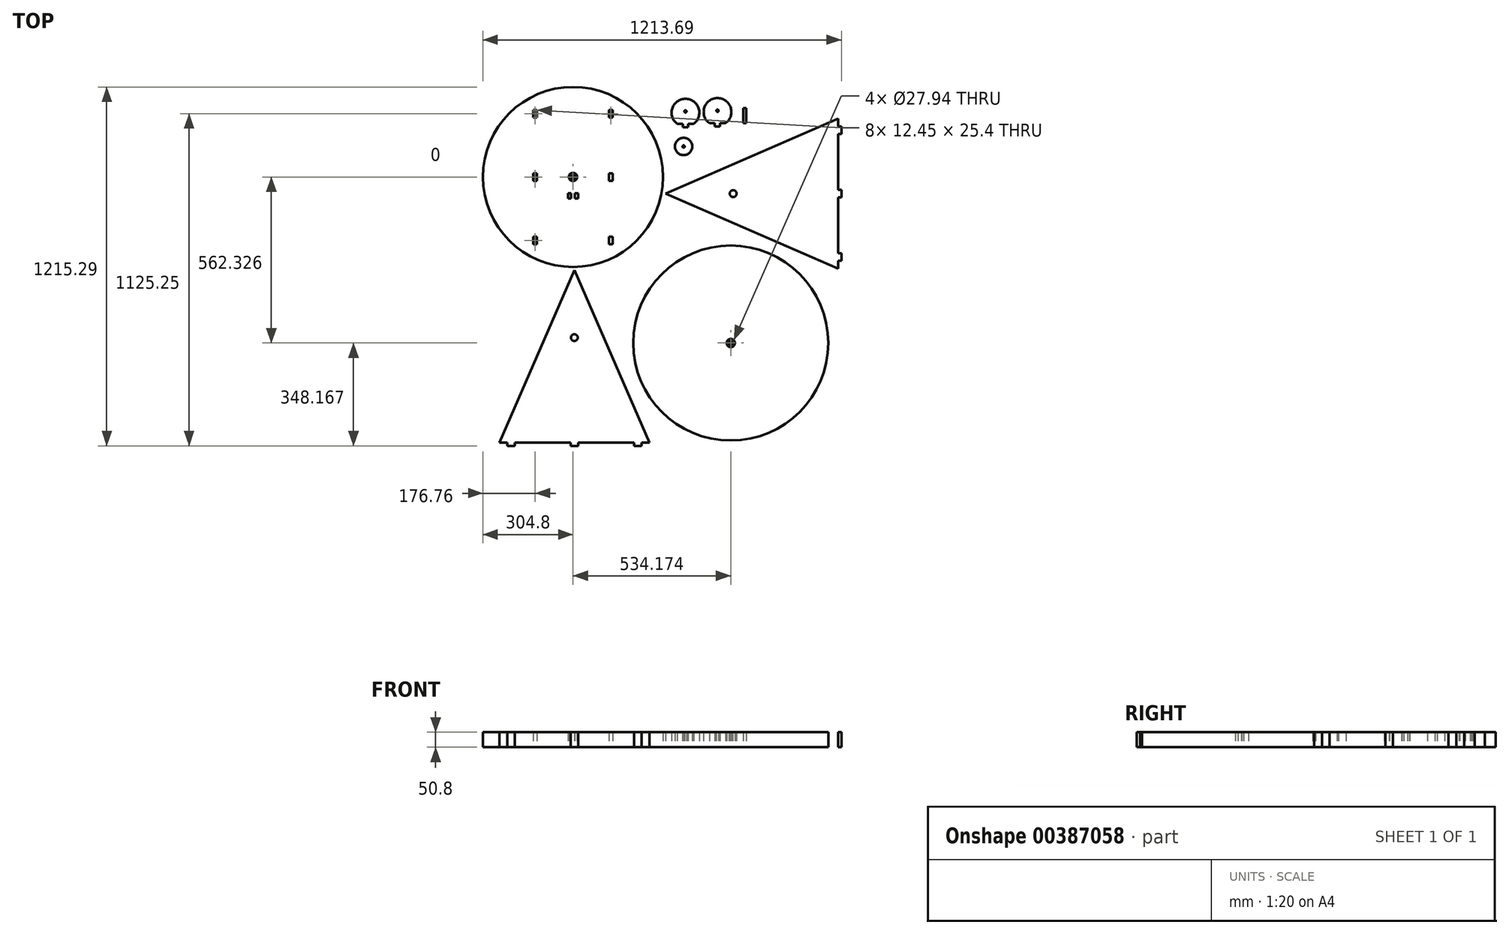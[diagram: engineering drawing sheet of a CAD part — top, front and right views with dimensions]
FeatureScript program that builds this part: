
annotation { "Feature Type Name" : "Feature", "Feature Type Description" : "" }
export const myFeature = defineFeature(function(context is Context, id is Id, definition is map)
    precondition{}
    {
        {
            var Q0;
            Q0=qCreatedBy(makeId("Top.planeOp"),FACE);
            var sketch = newSketch(context, id + "F0", { "sketchPlane" : qUnion([Q0])});
            skLineSegment(sketch, "E0.bottom", {"start": v(-756.4, 493.46) * mm, "end": v(462.8, 493.46) * mm});
            skLineSegment(sketch, "E0.top", {"start": v(-756.4, -725.6) * mm, "end": v(462.8, -725.6) * mm});
            skLineSegment(sketch, "E0.left", {"start": v(-756.4, 493.46) * mm, "end": v(-756.4, -725.6) * mm});
            skLineSegment(sketch, "E0.right", {"start": v(462.8, 493.46) * mm, "end": v(462.8, -725.6) * mm});
            skLineSegment(sketch, "E1", {"start": v(-146.8, -725.6) * mm, "end": v(-146.8, -116) * mm, "construction": true});
            skLineSegment(sketch, "E2", {"start": v(-146.8, -116) * mm, "end": v(462.8, -116.07) * mm, "construction": true});
            skLineSegment(sketch, "E3", {"start": v(-146.8, -116) * mm, "end": v(-756.4, -116.07) * mm, "construction": true});
            skLineSegment(sketch, "E4", {"start": v(-700.42, -725.6) * mm, "end": v(-192.42, -725.6) * mm});
            skLineSegment(sketch, "E5", {"start": v(-146.8, -116) * mm, "end": v(-146.8, 493.46) * mm, "construction": true});
            skLineSegment(sketch, "E6", {"start": v(447.02, -122.42) * mm, "end": v(447.02, -95.88) * mm});
            skPoint(sketch, "E7.endSnap0", {"position": v(447.02, 131.58) * mm});
            skLineSegment(sketch, "E8", {"start": v(447.02, 385.58) * mm, "end": v(-137.18, 131.58) * mm});
            skLineSegment(sketch, "E9", {"start": v(-137.18, 131.58) * mm, "end": v(447.02, -122.42) * mm});
            skLineSegment(sketch, "E10", {"start": v(447.02, 131.58) * mm, "end": v(91.42, 131.58) * mm, "construction": true});
            skCircle(sketch, "E11", {"center": v(91.42, 131.58) * mm, "radius": 11.58 * mm});
            skArc(sketch, "E12", {"start": v(-42.66, 367.48) * mm, "mid": v(-70.17, 452.57) * mm, "end": v(-97.67, 367.48) * mm});
            skLineSegment(sketch, "E13", {"start": v(-97.67, 367.48) * mm, "end": v(-79.2, 367.48) * mm});
            skLineSegment(sketch, "E14", {"start": v(-70.31, 367.48) * mm, "end": v(-70.31, 410.02) * mm, "construction": true});
            skArc(sketch, "E15", {"start": v(65.87, 369.96) * mm, "mid": v(38.37, 455.05) * mm, "end": v(10.86, 369.96) * mm});
            skLineSegment(sketch, "E16", {"start": v(38.37, 412.5) * mm, "end": v(38.37, 408.06) * mm, "construction": true});
            skLineSegment(sketch, "E17", {"start": v(10.86, 369.96) * mm, "end": v(29.48, 369.96) * mm});
            skLineSegment(sketch, "E18", {"start": v(38.37, 369.96) * mm, "end": v(38.37, 412.5) * mm, "construction": true});
            skPoint(sketch, "E19.orphan", {"position": v(-70.17, 452.57) * mm});
            skPoint(sketch, "E20.orphan", {"position": v(38.37, 455.05) * mm});
            skCircle(sketch, "E21", {"center": v(-76.43, 291.17) * mm, "radius": 29.21 * mm});
            skCircle(sketch, "E22", {"center": v(-76.43, 291.17) * mm, "radius": 3.82 * mm});
            skCircle(sketch, "E23", {"center": v(-70.31, 410.02) * mm, "radius": 3.82 * mm});
            skCircle(sketch, "E24", {"center": v(38.37, 412.5) * mm, "radius": 3.82 * mm});
            skLineSegment(sketch, "E25", {"start": v(125.4, 420.8) * mm, "end": v(135.57, 420.8) * mm});
            skLineSegment(sketch, "E26", {"start": v(135.57, 420.8) * mm, "end": v(135.57, 370) * mm});
            skLineSegment(sketch, "E27", {"start": v(135.57, 370) * mm, "end": v(125.4, 370) * mm});
            skLineSegment(sketch, "E28", {"start": v(125.4, 370) * mm, "end": v(125.4, 420.8) * mm});
            skLineSegment(sketch, "E29", {"start": v(447.02, -95.88) * mm, "end": v(457.94, -95.88) * mm});
            skLineSegment(sketch, "E30", {"start": v(457.94, -95.88) * mm, "end": v(457.94, -70.48) * mm});
            skLineSegment(sketch, "E31", {"start": v(457.94, -70.48) * mm, "end": v(447.02, -70.48) * mm});
            skLineSegment(sketch, "E32", {"start": v(447.02, 359.04) * mm, "end": v(457.94, 358.98) * mm});
            skLineSegment(sketch, "E33", {"start": v(457.94, 332.9) * mm, "end": v(447.02, 333.63) * mm});
            skLineSegment(sketch, "E34", {"start": v(-700.42, -711.69) * mm, "end": v(-673.88, -711.69) * mm});
            skPoint(sketch, "E35.endSnap0", {"position": v(-446.42, -711.69) * mm});
            skCircle(sketch, "E36", {"center": v(-450.95, 187.88) * mm, "radius": 304.8 * mm});
            skLineSegment(sketch, "E37", {"start": v(-192.42, -711.69) * mm, "end": v(-446.42, -127.49) * mm});
            skLineSegment(sketch, "E38", {"start": v(-446.42, -127.49) * mm, "end": v(-700.42, -711.69) * mm});
            skLineSegment(sketch, "E39", {"start": v(-673.88, -711.69) * mm, "end": v(-673.88, -722.61) * mm});
            skLineSegment(sketch, "E40", {"start": v(-673.88, -722.61) * mm, "end": v(-648.48, -722.61) * mm});
            skLineSegment(sketch, "E41", {"start": v(-648.48, -722.61) * mm, "end": v(-648.48, -711.69) * mm});
            skLineSegment(sketch, "E42", {"start": v(-218.97, -711.69) * mm, "end": v(-218.97, -722.61) * mm});
            skLineSegment(sketch, "E43", {"start": v(-218.97, -722.61) * mm, "end": v(-244.37, -722.61) * mm});
            skLineSegment(sketch, "E44", {"start": v(-244.37, -722.61) * mm, "end": v(-244.37, -711.69) * mm});
            skLineSegment(sketch, "E45.trimOffspring", {"start": v(-433.72, -711.69) * mm, "end": v(-244.37, -711.69) * mm});
            skLineSegment(sketch, "E46.trimOffspring", {"start": v(-648.48, -711.69) * mm, "end": v(-459.12, -711.69) * mm});
            skLineSegment(sketch, "E47.trimOffspring", {"start": v(-218.97, -711.69) * mm, "end": v(-192.42, -711.69) * mm});
            skLineSegment(sketch, "E48.trimOffspring", {"start": v(447.02, -70.48) * mm, "end": v(447.02, 111.03) * mm});
            skLineSegment(sketch, "E49.trimOffspring", {"start": v(447.02, 144.28) * mm, "end": v(447.02, 333.63) * mm});
            skLineSegment(sketch, "E50.trimOffspring", {"start": v(447.02, 359.04) * mm, "end": v(447.02, 385.58) * mm});
            skLineSegment(sketch, "E51", {"start": v(-446.42, -356.09) * mm, "end": v(-446.42, -711.69) * mm, "construction": true});
            skCircle(sketch, "E52", {"center": v(-446.42, -356.09) * mm, "radius": 11.58 * mm});
            skCircle(sketch, "E53", {"center": v(-450.95, 187.88) * mm, "radius": 6.1 * mm});
            skCircle(sketch, "E54", {"center": v(-450.95, 187.88) * mm, "radius": 13.97 * mm});
            skCircle(sketch, "E55", {"center": v(83.22, -374.44) * mm, "radius": 330.2 * mm});
            skCircle(sketch, "E56", {"center": v(83.22, -374.44) * mm, "radius": 6.1 * mm});
            skCircle(sketch, "E57", {"center": v(83.22, -374.44) * mm, "radius": 13.97 * mm});
            skLineSegment(sketch, "E58", {"start": v(-572.77, 467.28) * mm, "end": v(-572.77, 441.88) * mm, "construction": true});
            skLineSegment(sketch, "E59", {"start": v(-572.77, 441.88) * mm, "end": v(-572.77, 415.34) * mm, "construction": true});
            skLineSegment(sketch, "E60", {"start": v(-572.77, 415.34) * mm, "end": v(-572.77, 389.94) * mm, "construction": true});
            skLineSegment(sketch, "E61", {"start": v(-572.77, 200.58) * mm, "end": v(-572.77, 175.18) * mm, "construction": true});
            skLineSegment(sketch, "E62", {"start": v(-572.77, 415.34) * mm, "end": v(-572.77, 389.94) * mm});
            skLineSegment(sketch, "E63", {"start": v(-572.77, 200.58) * mm, "end": v(-572.77, 175.18) * mm});
            skLineSegment(sketch, "E64", {"start": v(-572.77, -14.18) * mm, "end": v(-572.77, -39.58) * mm, "construction": true});
            skLineSegment(sketch, "E65", {"start": v(-572.77, -39.58) * mm, "end": v(-572.77, -66.12) * mm, "construction": true});
            skLineSegment(sketch, "E66", {"start": v(-572.77, -66.12) * mm, "end": v(-572.75, -91.52) * mm, "construction": true});
            skLineSegment(sketch, "E67", {"start": v(-572.77, -14.18) * mm, "end": v(-572.77, -39.58) * mm});
            skLineSegment(sketch, "E68", {"start": v(-329.14, 467.29) * mm, "end": v(-329.15, 441.89) * mm, "construction": true});
            skLineSegment(sketch, "E69", {"start": v(-329.15, 441.89) * mm, "end": v(-329.15, 415.34) * mm, "construction": true});
            skLineSegment(sketch, "E70", {"start": v(-329.15, 415.34) * mm, "end": v(-329.15, 389.94) * mm, "construction": true});
            skLineSegment(sketch, "E71", {"start": v(-328.91, 200.59) * mm, "end": v(-328.96, 175.19) * mm, "construction": true});
            skLineSegment(sketch, "E72", {"start": v(-328.96, 175.19) * mm, "end": v(-328.91, 200.59) * mm});
            skLineSegment(sketch, "E73", {"start": v(-329.15, 389.94) * mm, "end": v(-329.15, 415.34) * mm});
            skLineSegment(sketch, "E74", {"start": v(-329.14, -14.2) * mm, "end": v(-329.14, -39.6) * mm, "construction": true});
            skLineSegment(sketch, "E75", {"start": v(-329.14, -39.6) * mm, "end": v(-329.14, -66.14) * mm, "construction": true});
            skLineSegment(sketch, "E76", {"start": v(-329.14, -66.14) * mm, "end": v(-329.13, -91.51) * mm, "construction": true});
            skLineSegment(sketch, "E77", {"start": v(-329.14, -14.2) * mm, "end": v(-329.14, -39.6) * mm});
            skLineSegment(sketch, "E78", {"start": v(-572.77, 389.94) * mm, "end": v(-585.21, 389.94) * mm});
            skLineSegment(sketch, "E79", {"start": v(-585.21, 389.94) * mm, "end": v(-585.21, 415.34) * mm});
            skLineSegment(sketch, "E80", {"start": v(-585.21, 415.34) * mm, "end": v(-572.77, 415.34) * mm});
            skLineSegment(sketch, "E81", {"start": v(-572.77, 175.18) * mm, "end": v(-585.21, 175.18) * mm});
            skLineSegment(sketch, "E82", {"start": v(-585.21, 175.18) * mm, "end": v(-585.21, 200.58) * mm});
            skLineSegment(sketch, "E83", {"start": v(-585.21, 200.58) * mm, "end": v(-572.77, 200.58) * mm});
            skLineSegment(sketch, "E84", {"start": v(-572.77, -39.58) * mm, "end": v(-585.21, -39.58) * mm});
            skLineSegment(sketch, "E85", {"start": v(-585.21, -39.58) * mm, "end": v(-585.21, -14.18) * mm});
            skLineSegment(sketch, "E86", {"start": v(-585.21, -14.18) * mm, "end": v(-572.77, -14.18) * mm});
            skLineSegment(sketch, "E87", {"start": v(-329.15, 389.94) * mm, "end": v(-316.7, 389.94) * mm});
            skLineSegment(sketch, "E88", {"start": v(-316.7, 389.94) * mm, "end": v(-316.7, 415.34) * mm});
            skLineSegment(sketch, "E89", {"start": v(-316.7, 415.34) * mm, "end": v(-329.15, 415.34) * mm});
            skLineSegment(sketch, "E90", {"start": v(-328.96, 175.19) * mm, "end": v(-316.52, 175.16) * mm});
            skLineSegment(sketch, "E91", {"start": v(-316.52, 175.16) * mm, "end": v(-316.52, 200.59) * mm});
            skLineSegment(sketch, "E92", {"start": v(-316.52, 200.59) * mm, "end": v(-328.91, 200.59) * mm});
            skLineSegment(sketch, "E93", {"start": v(-329.14, -39.6) * mm, "end": v(-316.52, -39.6) * mm});
            skLineSegment(sketch, "E94", {"start": v(-316.52, -39.6) * mm, "end": v(-316.52, -14.2) * mm});
            skLineSegment(sketch, "E95", {"start": v(-316.52, -14.2) * mm, "end": v(-329.14, -14.2) * mm});
            skLineSegment(sketch, "E96", {"start": v(457.94, 358.98) * mm, "end": v(457.94, 332.9) * mm});
            skLineSegment(sketch, "E97", {"start": v(447.02, 144.28) * mm, "end": v(457.94, 144.28) * mm});
            skLineSegment(sketch, "E98", {"start": v(457.94, 144.28) * mm, "end": v(457.94, 118.88) * mm});
            skLineSegment(sketch, "E99", {"start": v(457.94, 118.88) * mm, "end": v(447.02, 118.88) * mm});
            skLineSegment(sketch, "E100.trimOffspring", {"start": v(447.02, -70.48) * mm, "end": v(447.02, 118.88) * mm});
            skLineSegment(sketch, "E101", {"start": v(-433.72, -711.69) * mm, "end": v(-433.72, -722.61) * mm});
            skLineSegment(sketch, "E102", {"start": v(-433.72, -722.61) * mm, "end": v(-459.12, -722.61) * mm});
            skLineSegment(sketch, "E103", {"start": v(-459.12, -722.61) * mm, "end": v(-459.12, -711.69) * mm});
            skLineSegment(sketch, "E104", {"start": v(-572.77, 467.28) * mm, "end": v(-572.75, -91.52) * mm, "construction": true});
            skLineSegment(sketch, "E105", {"start": v(-329.14, 467.29) * mm, "end": v(-329.13, -91.51) * mm, "construction": true});
            skLineSegment(sketch, "E106", {"start": v(-61.42, 367.48) * mm, "end": v(-61.42, 356.55) * mm});
            skLineSegment(sketch, "E107", {"start": v(-61.42, 356.55) * mm, "end": v(-79.2, 356.55) * mm});
            skLineSegment(sketch, "E108", {"start": v(-79.2, 356.55) * mm, "end": v(-79.2, 367.48) * mm});
            skLineSegment(sketch, "E109", {"start": v(47.26, 369.96) * mm, "end": v(47.26, 359.04) * mm});
            skLineSegment(sketch, "E110", {"start": v(47.26, 359.04) * mm, "end": v(29.48, 359.04) * mm});
            skLineSegment(sketch, "E111", {"start": v(29.48, 359.04) * mm, "end": v(29.48, 369.96) * mm});
            skLineSegment(sketch, "E112.trimOffspring", {"start": v(47.26, 369.96) * mm, "end": v(65.87, 369.96) * mm});
            skLineSegment(sketch, "E113.trimOffspring", {"start": v(-61.42, 367.48) * mm, "end": v(-42.66, 367.48) * mm});
            skLineSegment(sketch, "E114", {"start": v(-450.95, 187.88) * mm, "end": v(-450.95, -116.92) * mm, "construction": true});
            skLineSegment(sketch, "E115", {"start": v(-450.95, 187.88) * mm, "end": v(-450.95, 124.38) * mm, "construction": true});
            skLineSegment(sketch, "E116", {"start": v(-450.95, 124.38) * mm, "end": v(-450.95, 142.67) * mm, "construction": true});
            skLineSegment(sketch, "E117", {"start": v(-450.95, 124.38) * mm, "end": v(-450.95, 104.8) * mm, "construction": true});
            skLineSegment(sketch, "E118", {"start": v(-462.5, 124.38) * mm, "end": v(-462.5, 133.27) * mm, "construction": true});
            skLineSegment(sketch, "E119", {"start": v(-462.5, 124.38) * mm, "end": v(-462.5, 115.5) * mm, "construction": true});
            skLineSegment(sketch, "E120", {"start": v(-462.5, 133.27) * mm, "end": v(-457.05, 133.27) * mm, "construction": true});
            skLineSegment(sketch, "E121", {"start": v(-462.5, 133.27) * mm, "end": v(-467.97, 133.27) * mm, "construction": true});
            skLineSegment(sketch, "E122", {"start": v(-467.97, 133.27) * mm, "end": v(-457.05, 133.27) * mm});
            skLineSegment(sketch, "E123", {"start": v(-457.05, 133.27) * mm, "end": v(-457.05, 115.5) * mm});
            skLineSegment(sketch, "E124", {"start": v(-457.05, 115.5) * mm, "end": v(-467.97, 115.5) * mm});
            skLineSegment(sketch, "E125", {"start": v(-467.97, 115.5) * mm, "end": v(-467.97, 133.27) * mm});
            skLineSegment(sketch, "E126", {"start": v(-439.4, 124.38) * mm, "end": v(-439.4, 115.5) * mm, "construction": true});
            skLineSegment(sketch, "E127", {"start": v(-439.4, 115.5) * mm, "end": v(-439.4, 133.27) * mm, "construction": true});
            skLineSegment(sketch, "E128", {"start": v(-439.4, 133.27) * mm, "end": v(-444.85, 133.27) * mm, "construction": true});
            skLineSegment(sketch, "E129", {"start": v(-439.4, 133.27) * mm, "end": v(-433.93, 133.27) * mm, "construction": true});
            skLineSegment(sketch, "E130", {"start": v(-444.85, 133.27) * mm, "end": v(-433.93, 133.27) * mm});
            skLineSegment(sketch, "E131", {"start": v(-433.93, 133.27) * mm, "end": v(-433.93, 115.5) * mm});
            skLineSegment(sketch, "E132", {"start": v(-433.93, 115.5) * mm, "end": v(-444.85, 115.5) * mm});
            skLineSegment(sketch, "E133", {"start": v(-444.85, 115.5) * mm, "end": v(-444.85, 133.27) * mm});
            skSolve(sketch);
        }
        {
            var Q0;
            Q0=makeQuery(id+"F0.imprint","IMPRINT",FACE,{"disambiguationData":[TD([[makeQuery(id+"F0.imprint","IMPRINT",EDGE,{"derivedFrom":sQuery(id+"F0.wireOp",EDGE,"E6")}),1.0]])]});
            var Q1;
            Q1=makeQuery(id+"F0.imprint","IMPRINT",FACE,{"disambiguationData":[TD([[makeQuery(id+"F0.imprint","IMPRINT",EDGE,{"derivedFrom":sQuery(id+"F0.wireOp",EDGE,"E21")}),1.0]])]});
            var Q2;
            Q2=makeQuery(id+"F0.imprint","IMPRINT",FACE,{"disambiguationData":[TD([[makeQuery(id+"F0.imprint","IMPRINT",EDGE,{"derivedFrom":sQuery(id+"F0.wireOp",EDGE,"E12")}),1.0]])]});
            var Q3;
            Q3=makeQuery(id+"F0.imprint","IMPRINT",FACE,{"disambiguationData":[TD([[makeQuery(id+"F0.imprint","IMPRINT",EDGE,{"derivedFrom":sQuery(id+"F0.wireOp",EDGE,"E15")}),1.0]])]});
            var Q4;
            Q4=makeQuery(id+"F0.imprint","IMPRINT",FACE,{"disambiguationData":[TD([[makeQuery(id+"F0.imprint","IMPRINT",EDGE,{"derivedFrom":sQuery(id+"F0.wireOp",EDGE,"E25")}),-1.0]])]});
            var Q5;
            Q5=makeQuery(id+"F0.imprint","IMPRINT",FACE,{"disambiguationData":[TD([[makeQuery(id+"F0.imprint","IMPRINT",EDGE,{"derivedFrom":sQuery(id+"F0.wireOp",EDGE,"E34")}),1.0]])]});
            var Q6;
            Q6=makeQuery(id+"F0.imprint","IMPRINT",FACE,{"disambiguationData":[TD([[makeQuery(id+"F0.imprint","IMPRINT",EDGE,{"derivedFrom":sQuery(id+"F0.wireOp",EDGE,"E53")}),-1.0]])]});
            var Q7;
            Q7=makeQuery(id+"F0.imprint","IMPRINT",FACE,{"disambiguationData":[TD([[makeQuery(id+"F0.imprint","IMPRINT",EDGE,{"derivedFrom":sQuery(id+"F0.wireOp",EDGE,"E56")}),-1.0]])]});
            var Q8;
            Q8=makeQuery(id+"F0.imprint","IMPRINT",FACE,{"disambiguationData":[TD([[makeQuery(id+"F0.imprint","IMPRINT",EDGE,{"derivedFrom":sQuery(id+"F0.wireOp",EDGE,"E8")}),1.0]])]});
            var Q9;
            Q9=makeQuery(id+"F0.imprint","IMPRINT",FACE,{"disambiguationData":[TD([[makeQuery(id+"F0.imprint","IMPRINT",EDGE,{"derivedFrom":sQuery(id+"F0.wireOp",EDGE,"E37")}),1.0]])]});
            extrude(context, id + "F1", {"entities" : qUnion([Q0, Q1, Q2, Q3, Q4, Q5, Q6, Q7, Q8, Q9]), "depth" : 50.8 * mm});
        }
        {
            var Q0;
            Q0=makeQuery(id+"F0.imprint","IMPRINT",FACE,{"disambiguationData":[TD([[makeQuery(id+"F0.imprint","IMPRINT",EDGE,{"derivedFrom":sQuery(id+"F0.wireOp",EDGE,"E36")}),1.0]])]});
            var Q1;
            Q1=makeQuery(id+"F0.imprint","IMPRINT",FACE,{"disambiguationData":[TD([[makeQuery(id+"F0.imprint","IMPRINT",EDGE,{"derivedFrom":sQuery(id+"F0.wireOp",EDGE,"E55")}),1.0]])]});
            extrude(context, id + "F2", {"entities" : qUnion([Q0, Q1]), "depth" : 50.8 * mm});
        }
    });
